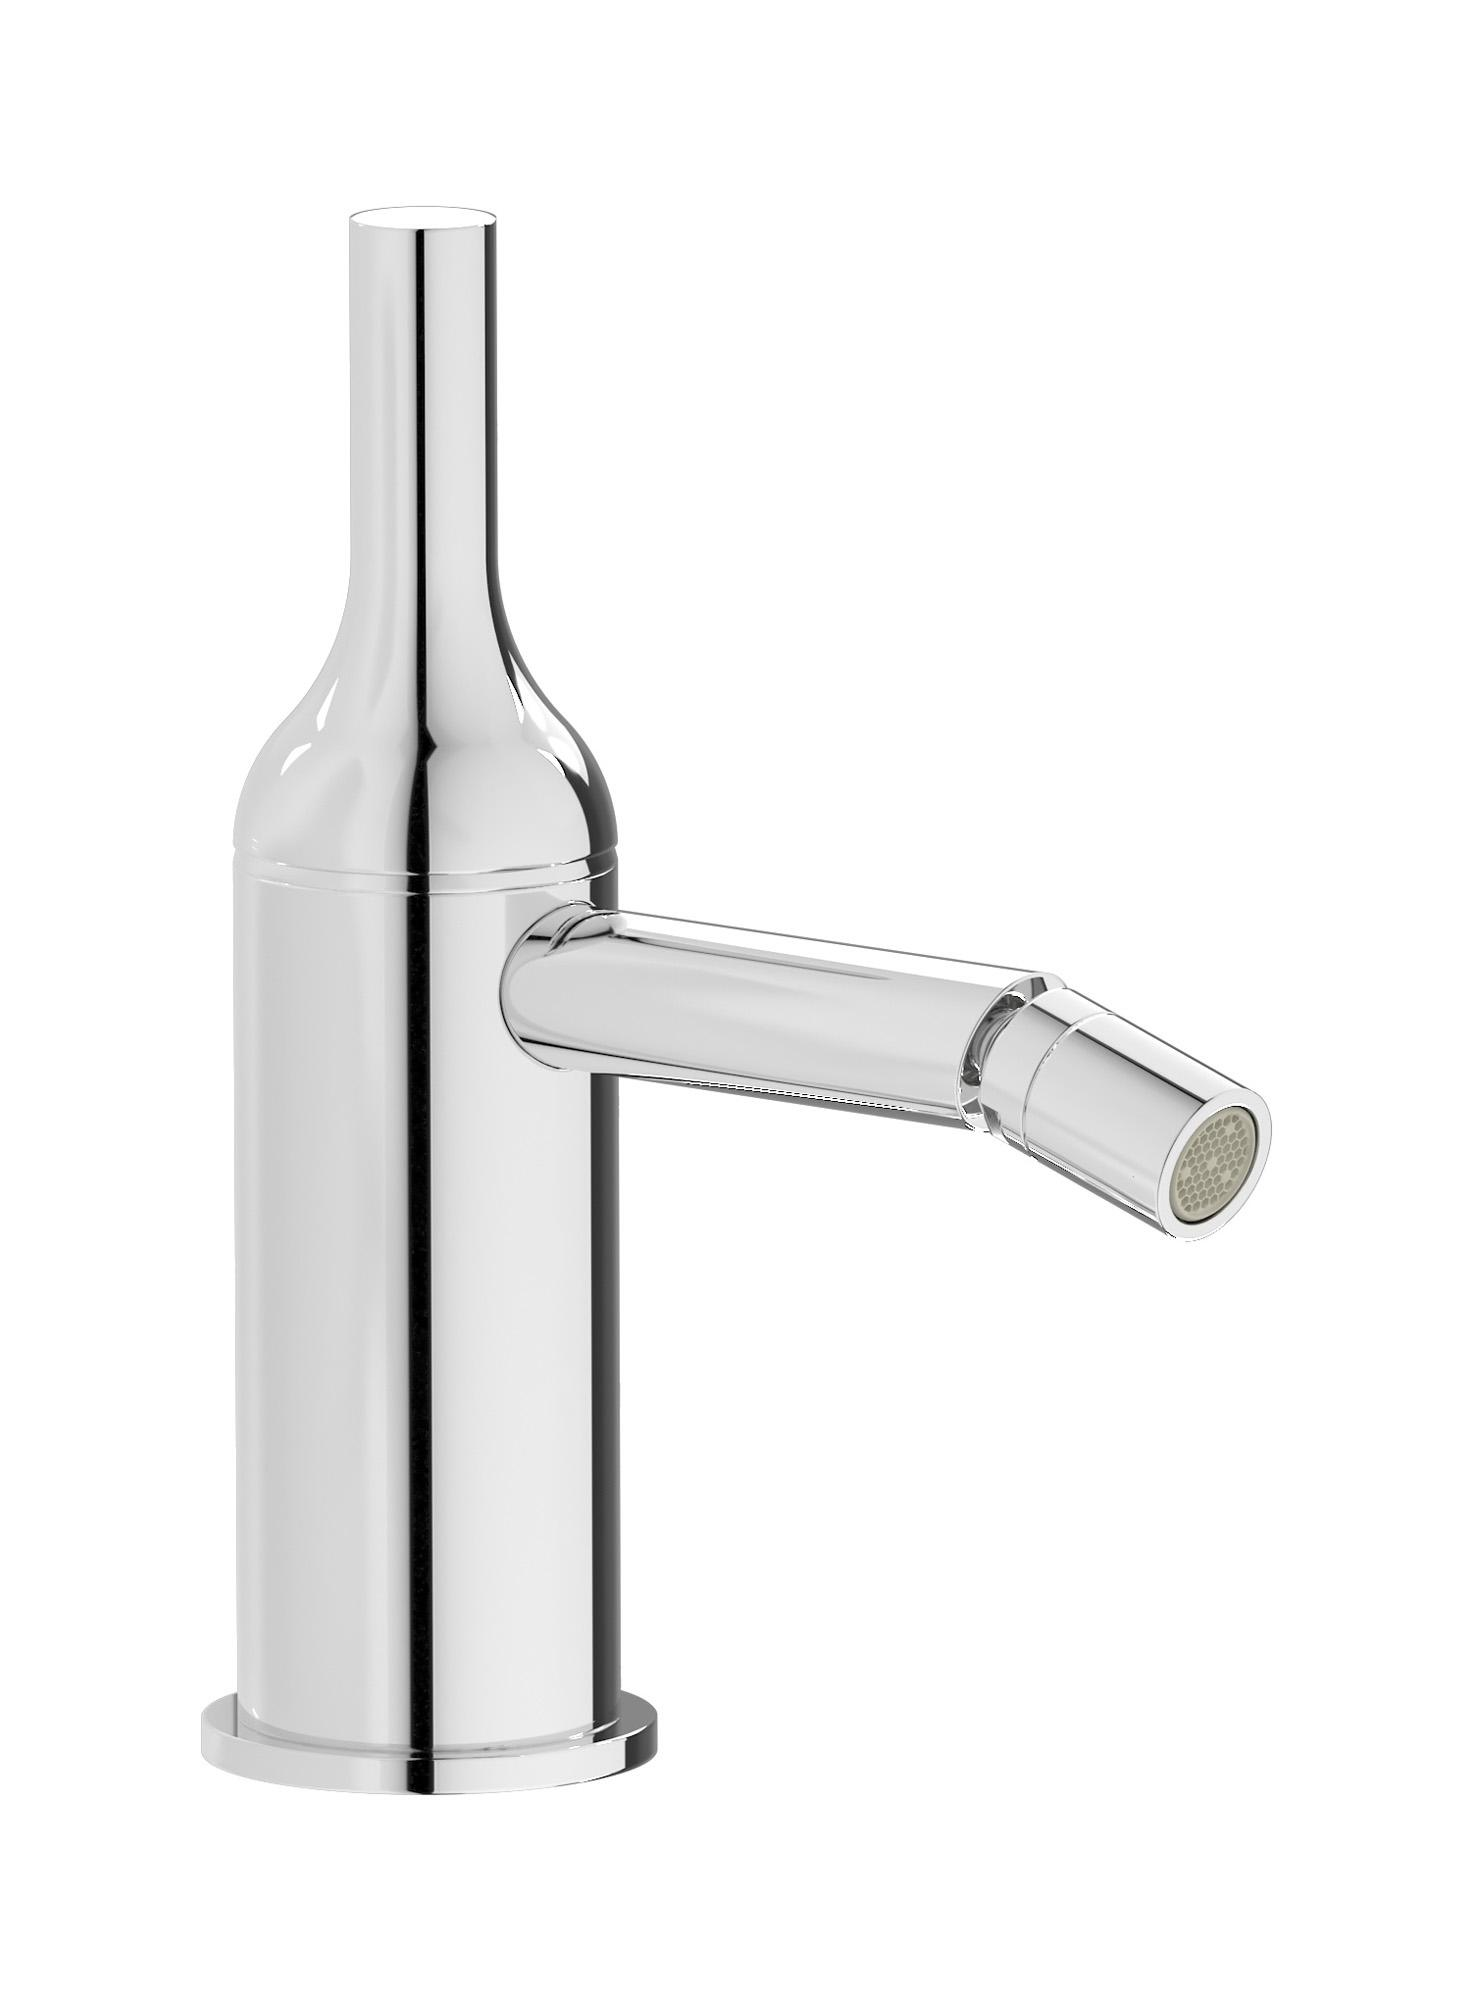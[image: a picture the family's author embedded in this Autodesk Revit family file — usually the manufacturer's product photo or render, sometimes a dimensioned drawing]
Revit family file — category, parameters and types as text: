
# Revit family: BI220
name_source: partatom
category: Apparecchi idraulici
units: mm (PartAtom-declared; Revit-internal decimal feet)

## family parameters
Basato su piano di lavoro = No
Condiviso = No
Mantieni orientamento annotazione = No
Numero OmniClass = 23.45.55.17
Punto di calcolo locali = No
Quota connettore circolare = Usa diametro
Sempre verticale = Sì
Taglio con vuoti quando caricato = No
Tipo di parte = Normale
Titolo OmniClass = Mixing Faucets

## types (4) — shared parameters
Cold water inlet = 10 mm  [stored 0.0328084 ft]
Commenti sul tipo = Bidet mixer
Connessione CW = No
Connessione HW = No
Connessione di scarico = No
Connessione di ventilazione = No
Descrizione = Monohole bidet mixer complete with drain
Hot water inlet = 10 mm  [stored 0.0328084 ft]
Produttore = IB Rubinetterie S.p.A.
URL = https://www.weareib.it
zero-valued in all types: Prospetto di default

## per-type parameters (varying)
| type | Finishes surface | Immagine tipo | Modello |
| Chrome | IB_Chrome | BI220CC.jpg | BI220CC |
| Brushed nickel | IB_Brushed nickel | BI220SS.jpg | BI220SS |
| Matt black | IB_matt black | BI220NP.jpg | BI220NP |
| Matt white | IB_matt white | BI220BO.jpg | BI220BO |

note: [stored X ft] marks values corroborated as IEEE doubles in the binary element streams (Revit-internal decimal feet)
